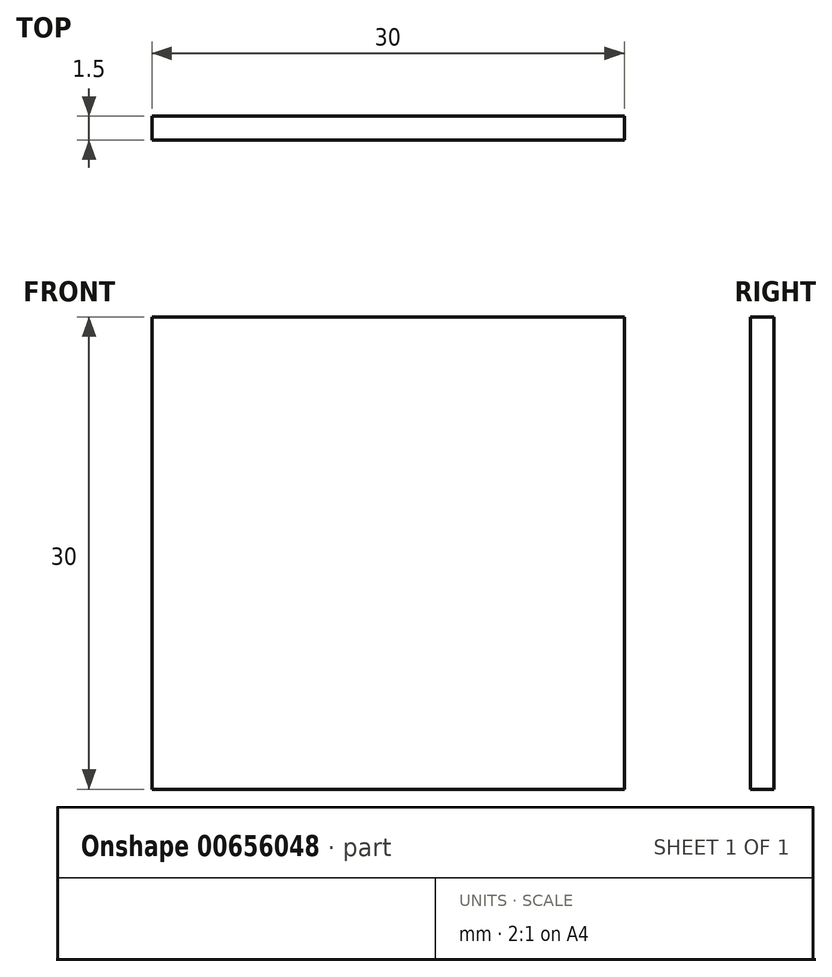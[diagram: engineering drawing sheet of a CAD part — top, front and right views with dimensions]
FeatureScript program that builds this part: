
annotation { "Feature Type Name" : "Feature", "Feature Type Description" : "" }
export const myFeature = defineFeature(function(context is Context, id is Id, definition is map)
    precondition{}
    {
        {
            var Q0;
            Q0=qCreatedBy(makeId("Front.planeOp"),FACE);
            var sketch = newSketch(context, id + "F0", { "sketchPlane" : qUnion([Q0])});
            skLineSegment(sketch, "E0.bottom", {"start": v(2.81, 0) * mm, "end": v(32.81, 0) * mm});
            skLineSegment(sketch, "E0.top", {"start": v(2.81, -30) * mm, "end": v(32.81, -30) * mm});
            skLineSegment(sketch, "E0.left", {"start": v(2.81, 0) * mm, "end": v(2.81, -30) * mm});
            skLineSegment(sketch, "E0.right", {"start": v(32.81, 0) * mm, "end": v(32.81, -30) * mm});
            skSolve(sketch);
        }
        {
            var Q0;
            Q0=makeQuery(id+"F0.imprint","IMPRINT",FACE,{"disambiguationData":[TD([[makeQuery(id+"F0.imprint","IMPRINT",EDGE,{"derivedFrom":sQuery(id+"F0.wireOp",EDGE,"E0.bottom")}),-1.0]])]});
            extrude(context, id + "F1", {"entities" : qUnion([Q0]), "depth" : 1.5 * mm, "offsetDistance" : 25.4 * mm});
        }
    });
